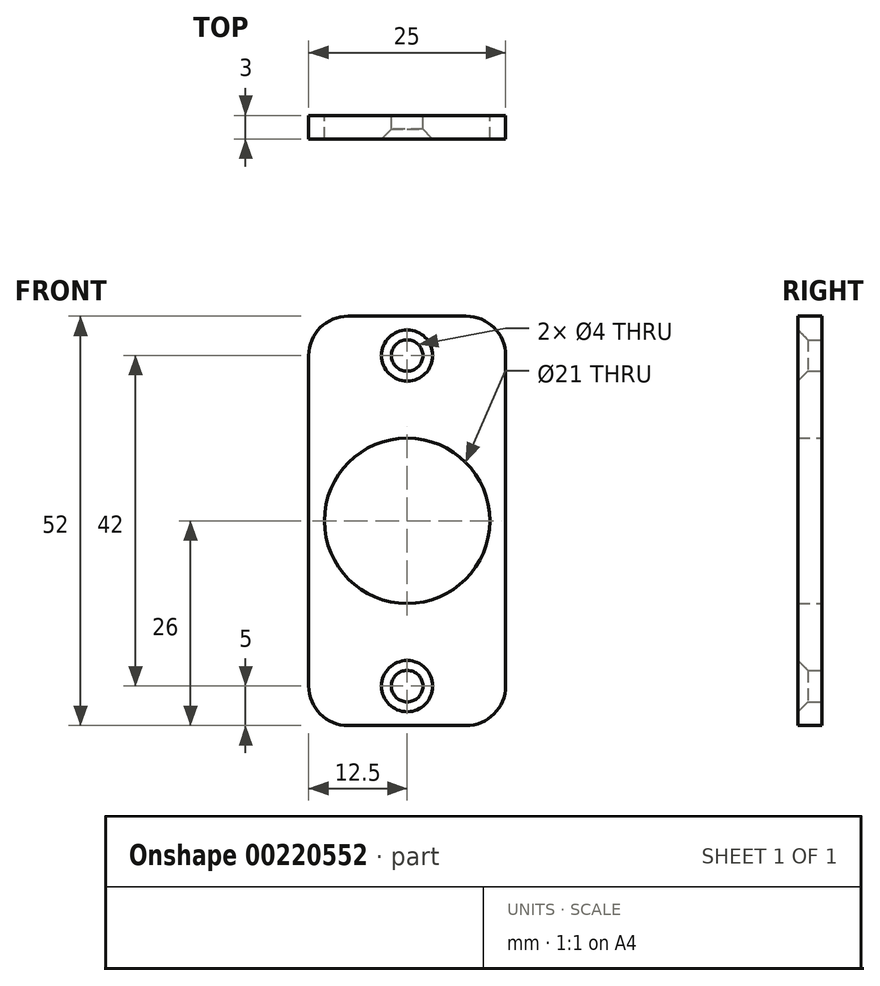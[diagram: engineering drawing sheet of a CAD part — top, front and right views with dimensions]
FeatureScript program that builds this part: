
annotation { "Feature Type Name" : "Feature", "Feature Type Description" : "" }
export const myFeature = defineFeature(function(context is Context, id is Id, definition is map)
    precondition{}
    {
        {
            var Q0;
            Q0=qCreatedBy(makeId("Front.planeOp"),FACE);
            var sketch = newSketch(context, id + "F0", { "sketchPlane" : qUnion([Q0])});
            skLineSegment(sketch, "E0", {"start": v(0, 0) * mm, "end": v(25, 0) * mm});
            skLineSegment(sketch, "E1", {"start": v(25, 0) * mm, "end": v(25, 52) * mm});
            skLineSegment(sketch, "E2", {"start": v(25, 52) * mm, "end": v(0, 52) * mm});
            skLineSegment(sketch, "E3", {"start": v(0, 52) * mm, "end": v(0, 0) * mm});
            skSolve(sketch);
        }
        {
            var Q0;
            Q0=makeQuery(id+"F0.imprint","IMPRINT",FACE,{"disambiguationData":[TD([[makeQuery(id+"F0.imprint","IMPRINT",EDGE,{"derivedFrom":sQuery(id+"F0.wireOp",EDGE,"E0")}),1.0]])]});
            extrude(context, id + "F1", {"entities" : qUnion([Q0]), "depth" : 3 * mm});
        }
        {
            var Q0;
            Q0=makeQuery(id+"F1.opExtrude","SWEPT_EDGE",EDGE,{"disambiguationData":[OSD([sQuery(id+"F0.wireOp",EDGE,"E1"),sQuery(id+"F0.wireOp",EDGE,"E2")])]});
            var Q1;
            Q1=makeQuery(id+"F1.opExtrude","SWEPT_EDGE",EDGE,{"disambiguationData":[OSD([sQuery(id+"F0.wireOp",EDGE,"E2"),sQuery(id+"F0.wireOp",EDGE,"E3")])]});
            var Q2;
            Q2=makeQuery(id+"F1.opExtrude","SWEPT_EDGE",EDGE,{"disambiguationData":[OSD([sQuery(id+"F0.wireOp",EDGE,"E0"),sQuery(id+"F0.wireOp",EDGE,"E3")])]});
            var Q3;
            Q3=makeQuery(id+"F1.opExtrude","SWEPT_EDGE",EDGE,{"disambiguationData":[OSD([sQuery(id+"F0.wireOp",EDGE,"E0"),sQuery(id+"F0.wireOp",EDGE,"E1")])]});
            fillet(context, id + "F2", {"entities" : qUnion([Q0, Q1, Q2, Q3]), "radius" : 5 * mm, "tangentPropagation" : true, "allowEdgeOverflow" : false});
        }
        {
            var Q0;
            Q0=makeQuery(id+"F1.opExtrude","CAP_FACE",FACE,{"disambiguationData":[OSD([sQuery(id+"F0.wireOp",EDGE,"E0"),sQuery(id+"F0.wireOp",EDGE,"E1"),sQuery(id+"F0.wireOp",EDGE,"E2"),sQuery(id+"F0.wireOp",EDGE,"E3")])],"isStart":false});
            var sketch = newSketch(context, id + "F3", { "sketchPlane" : qUnion([Q0])});
            skLineSegment(sketch, "E4", {"start": v(12.5, 52) * mm, "end": v(12.5, 0) * mm, "construction": true});
            skLineSegment(sketch, "E5", {"start": v(0, 26) * mm, "end": v(25, 26) * mm, "construction": true});
            skCircle(sketch, "E6", {"center": v(12.5, 26) * mm, "radius": 9 * mm});
            skCircle(sketch, "E7", {"center": v(12.5, 47) * mm, "radius": 2.25 * mm});
            skCircle(sketch, "E8.MirrorC", {"center": v(12.5, 5) * mm, "radius": 2.25 * mm});
            skSolve(sketch);
        }
        {
            var Q0;
            Q0=sQuery(id+"F3.wireOp",VERTEX,"E7.center");
            var Q1;
            Q1=sQuery(id+"F3.wireOp",VERTEX,"E8.MirrorC.center");
            var Q2;
            Q2=makeQuery(id+"F1.opExtrude","SWEPT_BODY",BODY,{"disambiguationData":[OSD([sQuery(id+"F0.wireOp",EDGE,"E0"),sQuery(id+"F0.wireOp",EDGE,"E1"),sQuery(id+"F0.wireOp",EDGE,"E2"),sQuery(id+"F0.wireOp",EDGE,"E3")])]});
            hole(context, id + "F4", {"style" : HoleStyle.C_SINK, "endStyle" : HoleEndStyle.THROUGH, "holeDiameter" : 4 * mm, "cSinkDiameter" : 6.5 * mm, "cSinkAngle" : 90 * degree, "locations" : qUnion([Q0, Q1]), "scope" : qUnion([Q2]), "isTappedThrough" : true, "startStyle" : HoleStartStyle.SKETCH});
        }
        {
            var Q0;
            Q0=sQuery(id+"F3.wireOp",VERTEX,"E6.center");
            var Q1;
            Q1=makeQuery(id+"F1.opExtrude","SWEPT_BODY",BODY,{"disambiguationData":[OSD([sQuery(id+"F0.wireOp",EDGE,"E0"),sQuery(id+"F0.wireOp",EDGE,"E1"),sQuery(id+"F0.wireOp",EDGE,"E2"),sQuery(id+"F0.wireOp",EDGE,"E3")])]});
            hole(context, id + "F5", {"style" : HoleStyle.SIMPLE, "endStyle" : HoleEndStyle.THROUGH, "holeDiameter" : 21 * mm, "locations" : qUnion([Q0]), "scope" : qUnion([Q1]), "isTappedThrough" : true, "startStyle" : HoleStartStyle.SKETCH});
        }
    });
